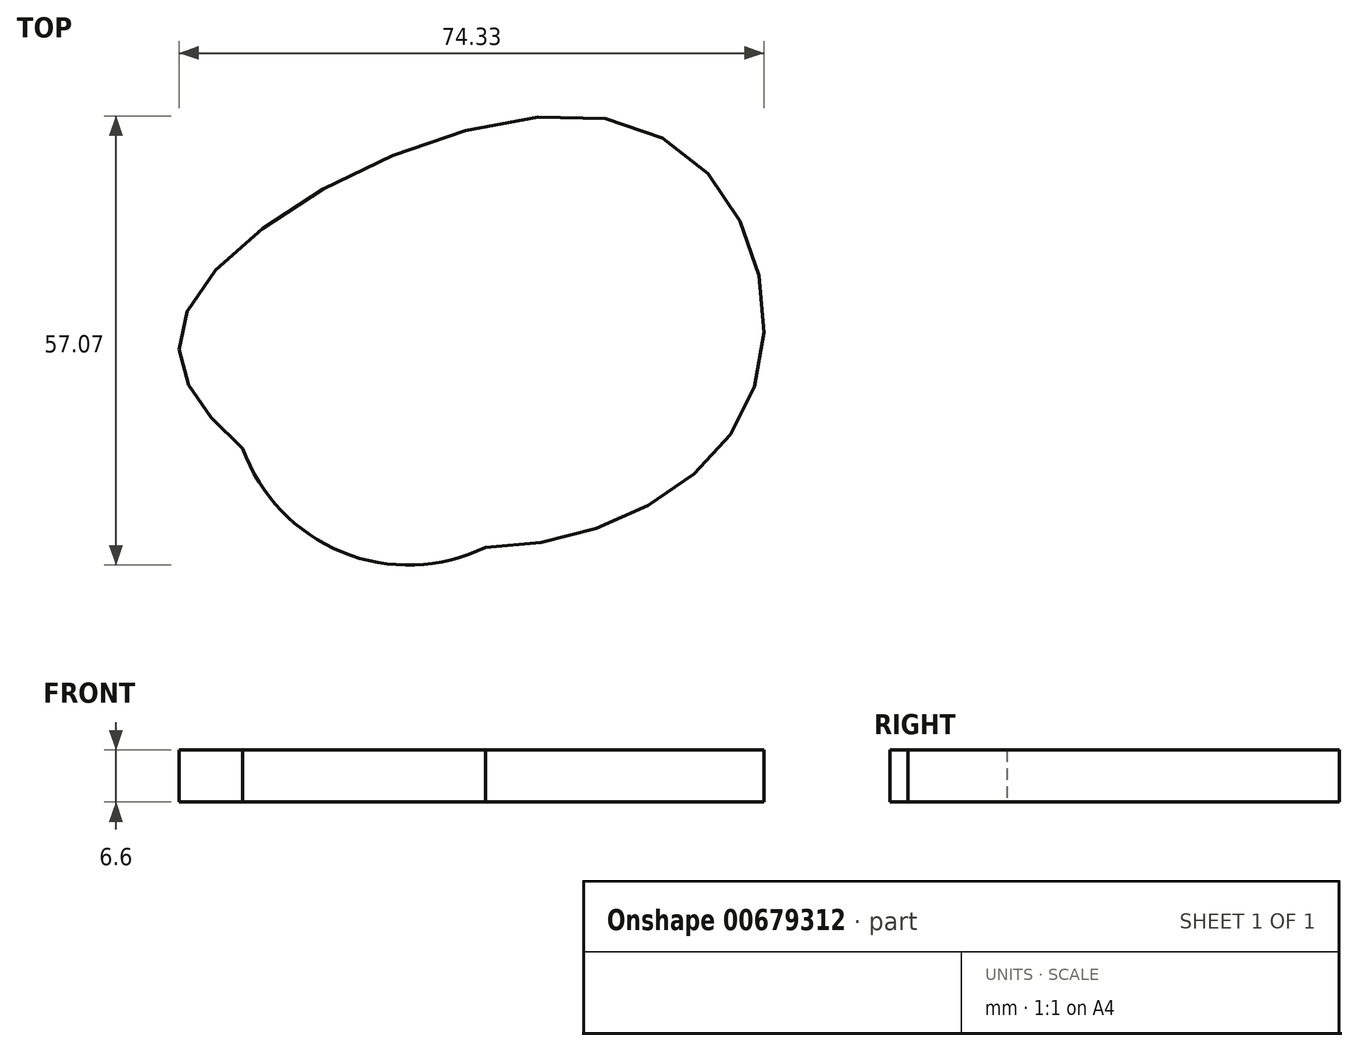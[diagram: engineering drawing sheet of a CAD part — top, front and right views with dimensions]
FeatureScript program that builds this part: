
annotation { "Feature Type Name" : "Feature", "Feature Type Description" : "" }
export const myFeature = defineFeature(function(context is Context, id is Id, definition is map)
    precondition{}
    {
        {
            var Q0;
            Q0=qCreatedBy(makeId("Top.planeOp"),FACE);
            var sketch = newSketch(context, id + "F0", { "sketchPlane" : qUnion([Q0])});
            skCircle(sketch, "E0", {"center": v(-34.08, 7.53) * mm, "radius": 22.36 * mm});
            skFitSpline(sketch, "E1", {"points": [v(-55.14, 0) * mm, v(-61.97, 17.93) * mm, v(-5.98, 41.17) * mm, v(9.52, 6.86) * mm, v(-24.27, -12.56) * mm, v(-55.14, 0) * mm]});
            skSolve(sketch);
        }
        {
            var Q0;
            {var subQ0=sQuery(id+"F0.wireOp",EDGE,"E1");var subQ1=sQuery(id+"F0.wireOp",EDGE,"E0");var subQ2=makeQuery(id+"F0.imprint","INTERSECT",VERTEX,{"disambiguationData":[OD(0.0)],"derivedFrom":[subQ1,subQ0]});Q0=makeQuery(id+"F0.imprint","IMPRINT",FACE,{"disambiguationData":[TD([[makeQuery(id+"F0.imprint","IMPRINT",EDGE,{"disambiguationData":[TD([[subQ2,1.0]])],"derivedFrom":subQ1}),1.0]])]});}
            var Q1;
            {var subQ0=sQuery(id+"F0.wireOp",EDGE,"E1");var subQ1=sQuery(id+"F0.wireOp",EDGE,"E0");var subQ2=makeQuery(id+"F0.imprint","INTERSECT",VERTEX,{"disambiguationData":[OD(0.0)],"derivedFrom":[subQ1,subQ0]});Q1=makeQuery(id+"F0.imprint","IMPRINT",FACE,{"disambiguationData":[TD([[makeQuery(id+"F0.imprint","IMPRINT",EDGE,{"disambiguationData":[TD([[subQ2,1.0]])],"derivedFrom":subQ1}),-1.0]])]});}
            var Q2;
            {var subQ0=sQuery(id+"F0.wireOp",EDGE,"E1");var subQ1=sQuery(id+"F0.wireOp",EDGE,"E0");var subQ2=makeQuery(id+"F0.imprint","INTERSECT",VERTEX,{"disambiguationData":[OD(0.0)],"derivedFrom":[subQ1,subQ0]});Q2=makeQuery(id+"F0.imprint","IMPRINT",FACE,{"disambiguationData":[TD([[makeQuery(id+"F0.imprint","IMPRINT",EDGE,{"disambiguationData":[TD([[subQ2,-1.0]])],"derivedFrom":subQ1}),1.0]])]});}
            extrude(context, id + "F1", {"entities" : qUnion([Q0, Q1, Q2]), "depth" : 6.6 * mm, "offsetDistance" : 25.4 * mm});
        }
    });
